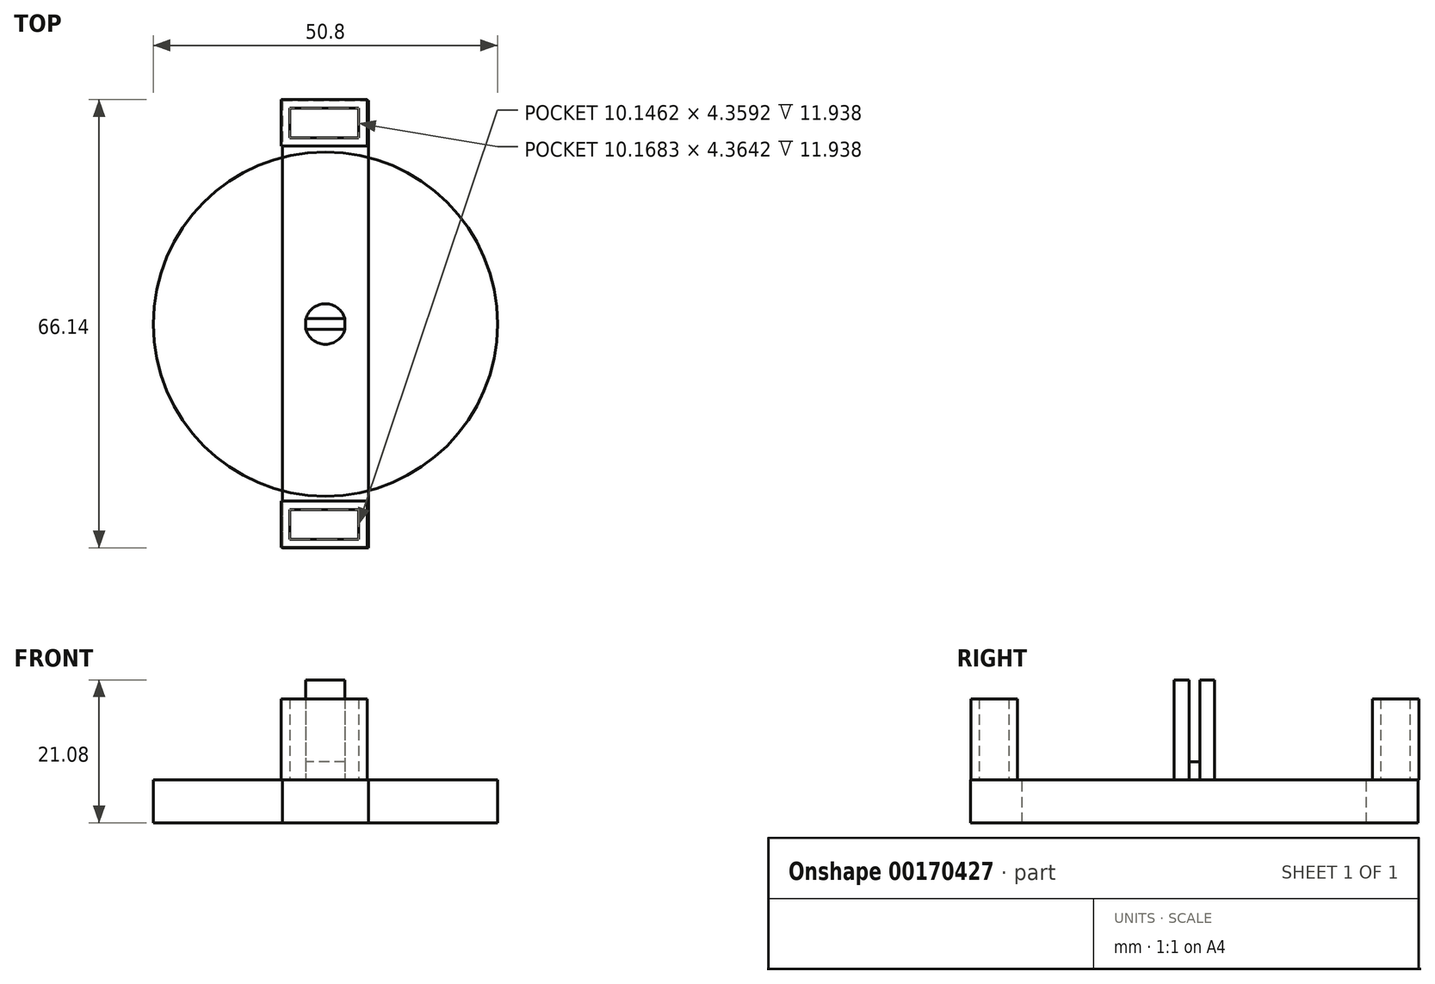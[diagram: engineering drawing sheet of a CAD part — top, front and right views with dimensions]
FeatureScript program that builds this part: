
annotation { "Feature Type Name" : "Feature", "Feature Type Description" : "" }
export const myFeature = defineFeature(function(context is Context, id is Id, definition is map)
    precondition{}
    {
        {
            var Q0;
            Q0=qCreatedBy(makeId("Top.planeOp"),FACE);
            var sketch = newSketch(context, id + "F0", { "sketchPlane" : qUnion([Q0])});
            skCircle(sketch, "E0", {"center": v(0, 0) * mm, "radius": 2.98 * mm});
            skSolve(sketch);
        }
        {
            var Q0;
            Q0 = qSketchRegion(id + "F0", true);
            extrude(context, id + "F1", {"entities" : qUnion([Q0]), "depth" : 14.73 * mm});
        }
        {
            var Q0;
            Q0=qCreatedBy(makeId("Top.planeOp"),FACE);
            var sketch = newSketch(context, id + "F2", { "sketchPlane" : qUnion([Q0])});
            skLineSegment(sketch, "E1", {"start": v(-4.59, -0.78) * mm, "end": v(3.11, -0.78) * mm});
            skLineSegment(sketch, "E2", {"start": v(-4.59, -0.78) * mm, "end": v(-4.59, 0.8) * mm});
            skLineSegment(sketch, "E3", {"start": v(-4.59, 0.8) * mm, "end": v(3.11, 0.8) * mm});
            skLineSegment(sketch, "E4", {"start": v(3.11, 0.8) * mm, "end": v(3.11, -0.78) * mm});
            skSolve(sketch);
        }
        {
            var Q0;
            Q0 = qSketchRegion(id + "F2", true);
            extrude(context, id + "F3", {"entities" : qUnion([Q0]), "operationType" : NewBodyOperationType.REMOVE, "depth" : 25.4 * mm});
        }
        {
            var Q0;
            Q0=qCreatedBy(makeId("Top.planeOp"),FACE);
            var sketch = newSketch(context, id + "F4", { "sketchPlane" : qUnion([Q0])});
            skCircle(sketch, "E5", {"center": v(0, 0) * mm, "radius": 25.4 * mm});
            skSolve(sketch);
        }
        {
            var Q0;
            Q0 = qSketchRegion(id + "F4", true);
            extrude(context, id + "F5", {"entities" : qUnion([Q0]), "oppositeDirection" : true, "depth" : 6.35 * mm});
        }
        {
            var Q0;
            Q0=qCreatedBy(makeId("Top.planeOp"),FACE);
            var sketch = newSketch(context, id + "F6", { "sketchPlane" : qUnion([Q0])});
            skLineSegment(sketch, "E6", {"start": v(0, 33.02) * mm, "end": v(-6.35, 33.02) * mm});
            skLineSegment(sketch, "E7", {"start": v(0, 33.02) * mm, "end": v(6.35, 33.02) * mm});
            skLineSegment(sketch, "E8", {"start": v(-6.35, 33.02) * mm, "end": v(-6.35, -33.02) * mm});
            skLineSegment(sketch, "E9", {"start": v(-6.35, -33.02) * mm, "end": v(6.35, -33.02) * mm});
            skLineSegment(sketch, "E10", {"start": v(6.35, 33.02) * mm, "end": v(6.35, -33.02) * mm});
            skSolve(sketch);
        }
        {
            var Q0;
            Q0 = qSketchRegion(id + "F6", true);
            extrude(context, id + "F7", {"entities" : qUnion([Q0]), "oppositeDirection" : true, "depth" : 6.35 * mm});
        }
        {
            var Q0;
            Q0=qCreatedBy(makeId("Top.planeOp"),FACE);
            var sketch = newSketch(context, id + "F8", { "sketchPlane" : qUnion([Q0])});
            skLineSegment(sketch, "E11.bottom", {"start": v(6.2, 33.12) * mm, "end": v(-6.5, 33.12) * mm});
            skLineSegment(sketch, "E11.top", {"start": v(6.2, 26.26) * mm, "end": v(-6.5, 26.26) * mm});
            skLineSegment(sketch, "E11.left", {"start": v(6.2, 33.12) * mm, "end": v(6.2, 26.26) * mm});
            skLineSegment(sketch, "E11.right", {"start": v(-6.5, 33.12) * mm, "end": v(-6.5, 26.26) * mm});
            skPoint(sketch, "E12.firstSnap0", {"position": v(6.2, 29.69) * mm});
            skLineSegment(sketch, "E12.bottom", {"start": v(6.2, -32.96) * mm, "end": v(-6.5, -32.96) * mm});
            skLineSegment(sketch, "E12.top", {"start": v(6.2, -26.1) * mm, "end": v(-6.5, -26.1) * mm});
            skLineSegment(sketch, "E12.left", {"start": v(6.2, -32.96) * mm, "end": v(6.2, -26.1) * mm});
            skLineSegment(sketch, "E12.right", {"start": v(-6.5, -32.96) * mm, "end": v(-6.5, -26.1) * mm});
            skSolve(sketch);
        }
        {
            var Q0;
            Q0 = qSketchRegion(id + "F8", true);
            extrude(context, id + "F9", {"entities" : qUnion([Q0]), "operationType" : NewBodyOperationType.ADD, "depth" : 11.94 * mm});
        }
        {
            var Q0;
            Q0=qCreatedBy(makeId("Top.planeOp"),FACE);
            var sketch = newSketch(context, id + "F10", { "sketchPlane" : qUnion([Q0])});
            skLineSegment(sketch, "E13", {"start": v(4.87, -29.43) * mm, "end": v(4.87, -31.76) * mm});
            skLineSegment(sketch, "E14", {"start": v(4.87, -31.76) * mm, "end": v(-5.28, -31.76) * mm});
            skPoint(sketch, "E15.end.orphan", {"position": v(-2.16, -31.76) * mm});
            skLineSegment(sketch, "E16", {"start": v(-5.28, -29.45) * mm, "end": v(-5.28, -31.76) * mm});
            skLineSegment(sketch, "E17", {"start": v(-1.85, -27.4) * mm, "end": v(-5.28, -27.4) * mm});
            skLineSegment(sketch, "E18", {"start": v(-5.28, -29.45) * mm, "end": v(-5.28, -27.4) * mm});
            skLineSegment(sketch, "E19", {"start": v(4.87, -29.43) * mm, "end": v(4.87, -27.4) * mm});
            skLineSegment(sketch, "E20", {"start": v(-1.85, -27.4) * mm, "end": v(4.87, -27.4) * mm});
            skSolve(sketch);
        }
        {
            var Q0;
            Q0 = qSketchRegion(id + "F10", true);
            extrude(context, id + "F11", {"entities" : qUnion([Q0]), "operationType" : NewBodyOperationType.REMOVE, "depth" : 25.4 * mm});
        }
        {
            var Q0;
            Q0=qCreatedBy(makeId("Top.planeOp"),FACE);
            var sketch = newSketch(context, id + "F12", { "sketchPlane" : qUnion([Q0])});
            skLineSegment(sketch, "E21", {"start": v(-1.72, 27.48) * mm, "end": v(4.9, 27.48) * mm});
            skLineSegment(sketch, "E22", {"start": v(-1.72, 27.48) * mm, "end": v(-5.27, 27.48) * mm});
            skLineSegment(sketch, "E23", {"start": v(-5.27, 29.54) * mm, "end": v(-5.27, 27.48) * mm});
            skLineSegment(sketch, "E24", {"start": v(-0.82, 31.84) * mm, "end": v(-5.27, 31.84) * mm});
            skLineSegment(sketch, "E25", {"start": v(-5.27, 29.54) * mm, "end": v(-5.27, 31.84) * mm});
            skLineSegment(sketch, "E26", {"start": v(-0.82, 31.84) * mm, "end": v(4.9, 31.84) * mm});
            skLineSegment(sketch, "E27", {"start": v(4.9, 29.9) * mm, "end": v(4.9, 27.48) * mm});
            skLineSegment(sketch, "E28", {"start": v(4.9, 29.9) * mm, "end": v(4.9, 31.84) * mm});
            skSolve(sketch);
        }
        {
            var Q0;
            Q0 = qSketchRegion(id + "F12", true);
            extrude(context, id + "F13", {"entities" : qUnion([Q0]), "operationType" : NewBodyOperationType.REMOVE, "depth" : 25.4 * mm});
        }
        {
            var Q0;
            Q0=makeQuery(id+"F5.opExtrude","CAP_FACE",FACE,{"disambiguationData":[OSD([sQuery(id+"F4.wireOp",EDGE,"E5")])],"isStart":true});
            var sketch = newSketch(context, id + "F14", { "sketchPlane" : qUnion([Q0])});
            skLineSegment(sketch, "E29.bottom", {"start": v(2.86, 0.8) * mm, "end": v(-2.88, 0.8) * mm});
            skLineSegment(sketch, "E29.top", {"start": v(2.86, -0.78) * mm, "end": v(-2.88, -0.78) * mm});
            skLineSegment(sketch, "E29.left", {"start": v(2.86, 0.8) * mm, "end": v(2.86, -0.78) * mm});
            skLineSegment(sketch, "E29.right", {"start": v(-2.88, 0.8) * mm, "end": v(-2.88, -0.78) * mm});
            skSolve(sketch);
        }
        {
            var Q0;
            Q0 = qSketchRegion(id + "F14", true);
            extrude(context, id + "F15", {"entities" : qUnion([Q0]), "depth" : 2.67 * mm});
        }
    });
